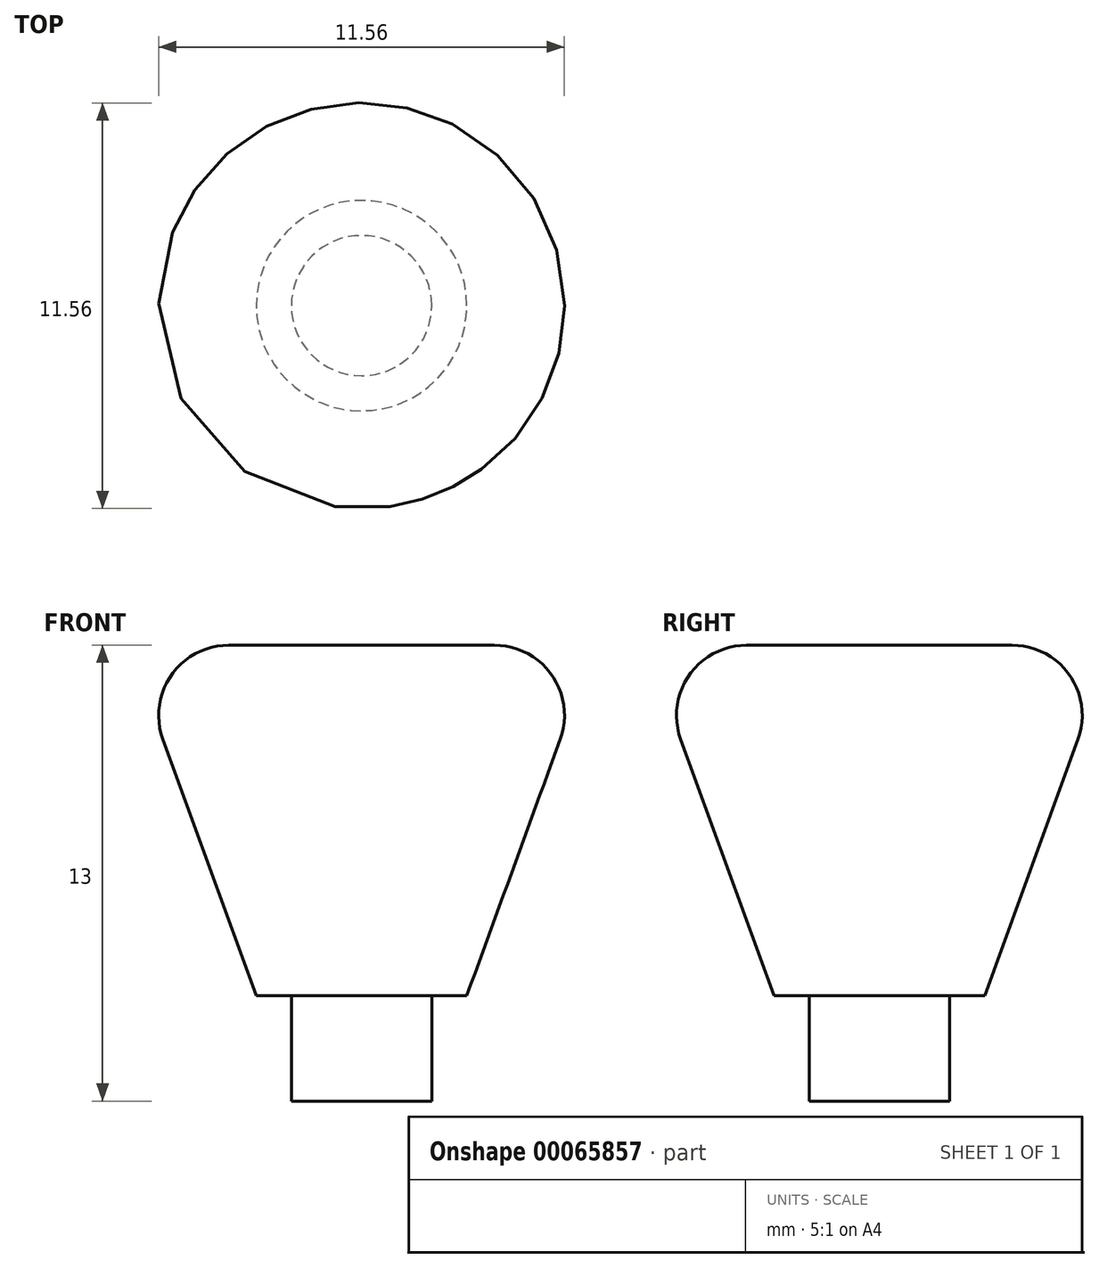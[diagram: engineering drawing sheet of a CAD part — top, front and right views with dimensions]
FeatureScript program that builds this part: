
annotation { "Feature Type Name" : "Feature", "Feature Type Description" : "" }
export const myFeature = defineFeature(function(context is Context, id is Id, definition is map)
    precondition{}
    {
        {
            var Q0;
            Q0=qCreatedBy(makeId("Top.planeOp"),FACE);
            var sketch = newSketch(context, id + "F0", { "sketchPlane" : qUnion([Q0])});
            skCircle(sketch, "E0", {"center": v(0, 0) * mm, "radius": 3 * mm});
            skSolve(sketch);
        }
        {
            var Q0;
            Q0 = qSketchRegion(id + "F0", true);
            extrude(context, id + "F1", {"entities" : qUnion([Q0]), "depth" : 10 * mm, "hasDraft" : true, "draftAngle" : 20 * degree});
        }
        {
            var Q0;
            Q0=makeQuery(id+"F1.opExtrude","CAP_EDGE",EDGE,{"disambiguationData":[OSD([sQuery(id+"F0.wireOp",EDGE,"E0")])],"isStart":false});
            fillet(context, id + "F2", {"entities" : qUnion([Q0]), "radius" : 2 * mm, "tangentPropagation" : true, "allowEdgeOverflow" : false});
        }
        {
            var Q0;
            Q0=makeQuery(id+"F1.opExtrude","CAP_FACE",FACE,{"disambiguationData":[OSD([sQuery(id+"F0.wireOp",EDGE,"E0")])],"isStart":true});
            var sketch = newSketch(context, id + "F3", { "sketchPlane" : qUnion([Q0])});
            skCircle(sketch, "E1", {"center": v(0, 0) * mm, "radius": 2 * mm});
            skSolve(sketch);
        }
        {
            var Q0;
            Q0 = qSketchRegion(id + "F3", true);
            extrude(context, id + "F4", {"entities" : qUnion([Q0]), "operationType" : NewBodyOperationType.ADD, "depth" : 3 * mm});
        }
    });
